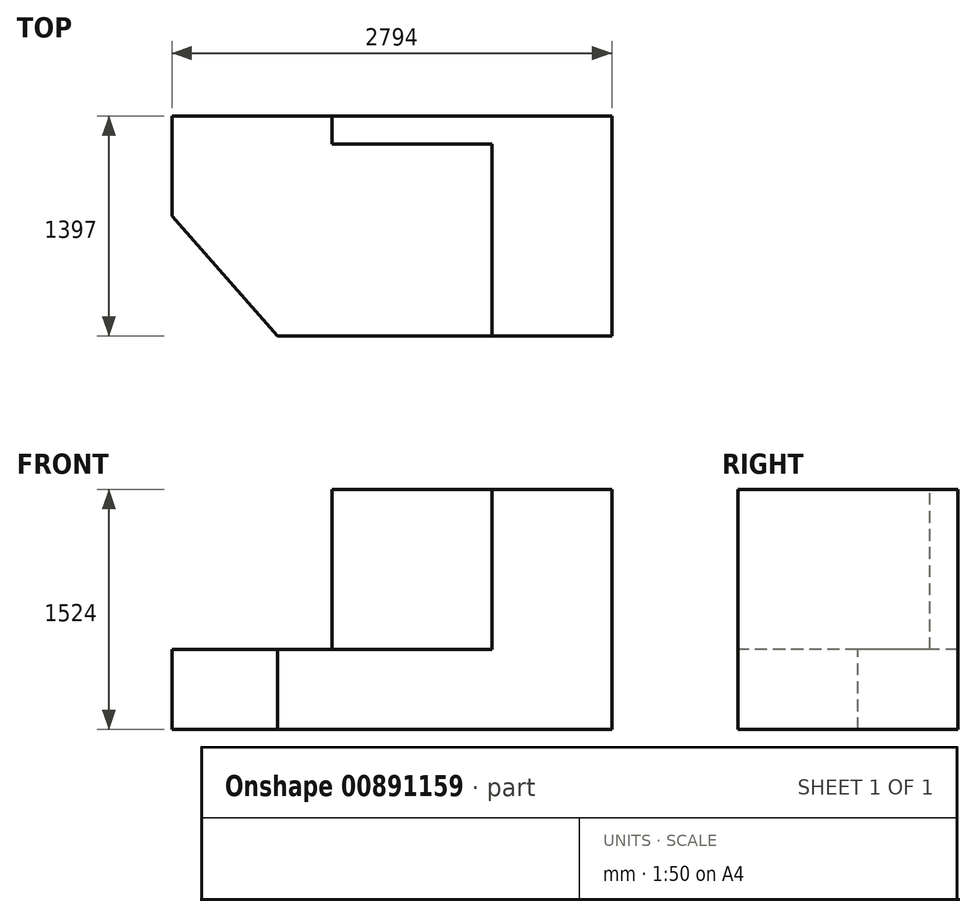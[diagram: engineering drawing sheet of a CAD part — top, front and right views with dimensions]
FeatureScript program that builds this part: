
annotation { "Feature Type Name" : "Feature", "Feature Type Description" : "" }
export const myFeature = defineFeature(function(context is Context, id is Id, definition is map)
    precondition{}
    {
        {
            var Q0;
            Q0=qCreatedBy(makeId("Top.planeOp"),FACE);
            var sketch = newSketch(context, id + "F0", { "sketchPlane" : qUnion([Q0])});
            skLineSegment(sketch, "E0.bottom", {"start": v(0, 0) * mm, "end": v(-2794, 0) * mm});
            skLineSegment(sketch, "E0.top", {"start": v(0, 1397) * mm, "end": v(-2794, 1397) * mm});
            skLineSegment(sketch, "E0.left", {"start": v(0, 0) * mm, "end": v(0, 1397) * mm});
            skLineSegment(sketch, "E0.right", {"start": v(-2794, 0) * mm, "end": v(-2794, 1397) * mm});
            skSolve(sketch);
        }
        {
            var Q0;
            Q0 = qSketchRegion(id + "F0", true);
            extrude(context, id + "F1", {"entities" : qUnion([Q0]), "depth" : 1524 * mm, "offsetDistance" : 25.4 * mm});
        }
        {
            var Q0;
            Q0=makeQuery(id+"F1.opExtrude","CAP_FACE",FACE,{"disambiguationData":[OSD([sQuery(id+"F0.wireOp",EDGE,"E0.bottom"),sQuery(id+"F0.wireOp",EDGE,"E0.top"),sQuery(id+"F0.wireOp",EDGE,"E0.left"),sQuery(id+"F0.wireOp",EDGE,"E0.right")])],"isStart":false});
            var sketch = newSketch(context, id + "F2", { "sketchPlane" : qUnion([Q0])});
            skLineSegment(sketch, "E1.bottom", {"start": v(-1778, 1397) * mm, "end": v(0, 1397) * mm});
            skLineSegment(sketch, "E1.top", {"start": v(-1778, 1219.2) * mm, "end": v(0, 1219.2) * mm});
            skLineSegment(sketch, "E1.left", {"start": v(-1778, 1397) * mm, "end": v(-1778, 1219.2) * mm});
            skLineSegment(sketch, "E1.right", {"start": v(0, 1397) * mm, "end": v(0, 1219.2) * mm});
            skSolve(sketch);
        }
        {
            var Q0;
            {var subQ4=sQuery(id+"F2.wireOp",EDGE,"E1.top");Q0=makeQuery(id+"F2.imprint","IMPRINT",FACE,{"disambiguationData":[TD([[makeQuery(id+"F2.imprint","IMPRINT",EDGE,{"derivedFrom":subQ4}),-1.0]])]});}
            var sketch = newSketch(context, id + "F3", { "sketchPlane" : qUnion([Q0])});
            skLineSegment(sketch, "E2.bottom", {"start": v(-762, 1016) * mm, "end": v(0, 1016) * mm});
            skLineSegment(sketch, "E2.top", {"start": v(-762, 0) * mm, "end": v(0, 0) * mm});
            skLineSegment(sketch, "E2.left", {"start": v(-762, 1016) * mm, "end": v(-762, 0) * mm});
            skLineSegment(sketch, "E2.right", {"start": v(0, 1016) * mm, "end": v(0, 0) * mm});
            skLineSegment(sketch, "E3.bottom", {"start": v(-1775.76, 1225.1) * mm, "end": v(-762, 1225.1) * mm});
            skLineSegment(sketch, "E3.top", {"start": v(-1775.76, 0) * mm, "end": v(-762, 0) * mm});
            skLineSegment(sketch, "E3.left", {"start": v(-1775.76, 1225.1) * mm, "end": v(-1775.76, 0) * mm});
            skLineSegment(sketch, "E3.right", {"start": v(-762, 1225.1) * mm, "end": v(-762, 0) * mm});
            skSolve(sketch);
        }
        {
            var Q0;
            {var subQ5=sQuery(id+"F3.wireOp",EDGE,"E3.top");Q0=makeQuery(id+"F3.imprint","IMPRINT",FACE,{"disambiguationData":[TD([[makeQuery(id+"F3.imprint","IMPRINT",EDGE,{"derivedFrom":subQ5}),-1.0]])]});}
            extrude(context, id + "F4", {"entities" : qUnion([Q0]), "operationType" : NewBodyOperationType.REMOVE, "oppositeDirection" : true, "depth" : 1016 * mm, "offsetDistance" : 25.4 * mm});
        }
        {
            var Q0;
            Q0=makeQuery(id+"F1.opExtrude","SWEPT_FACE",FACE,{"disambiguationData":[OSD([sQuery(id+"F0.wireOp",EDGE,"E0.bottom")])]});
            var sketch = newSketch(context, id + "F5", { "sketchPlane" : qUnion([Q0])});
            skLineSegment(sketch, "E4.bottom", {"start": v(-1775.76, 508) * mm, "end": v(-2794, 508) * mm});
            skLineSegment(sketch, "E4.top", {"start": v(-1775.76, 1524) * mm, "end": v(-2794, 1524) * mm});
            skLineSegment(sketch, "E4.left", {"start": v(-1775.76, 508) * mm, "end": v(-1775.76, 1524) * mm});
            skLineSegment(sketch, "E4.right", {"start": v(-2794, 508) * mm, "end": v(-2794, 1524) * mm});
            skSolve(sketch);
        }
        {
            var Q0;
            Q0=makeQuery(id+"F5.imprint","IMPRINT",FACE,{"disambiguationData":[TD([[makeQuery(id+"F5.imprint","IMPRINT",EDGE,{"derivedFrom":sQuery(id+"F5.wireOp",EDGE,"E4.bottom")}),-1.0]])]});
            extrude(context, id + "F6", {"entities" : qUnion([Q0]), "operationType" : NewBodyOperationType.REMOVE, "oppositeDirection" : true, "depth" : 3329.94 * mm, "offsetDistance" : 25.4 * mm});
        }
        {
            var Q0;
            Q0=makeQuery(id+"F6.boolean.opBoolean","MERGE",FACE,{"derivedFrom":[makeQuery(id+"F4.boolean.opBoolean","COPY",FACE,{"derivedFrom":makeQuery(id+"F4.opExtrude","CAP_FACE",FACE,{"disambiguationData":[OSD([sQuery(id+"F2.wireOp",EDGE,"E1.top"),sQuery(id+"F3.wireOp",EDGE,"E3.top"),sQuery(id+"F3.wireOp",EDGE,"E3.left"),sQuery(id+"F3.wireOp",EDGE,"E3.right")])],"isStart":false})})],"fromTools":[makeQuery(id+"F6.opExtrude","SWEPT_FACE",FACE,{"disambiguationData":[OSD([sQuery(id+"F5.wireOp",EDGE,"E4.bottom")])]})]});
            var sketch = newSketch(context, id + "F7", { "sketchPlane" : qUnion([Q0])});
            skLineSegment(sketch, "E5", {"start": v(-2794, 1397) * mm, "end": v(-2794, 762) * mm});
            skLineSegment(sketch, "E6", {"start": v(-2794, 762) * mm, "end": v(-2121.98, 0) * mm});
            skSolve(sketch);
        }
        {
            var Q0;
            {var subQ0=sQuery(id+"F7.wireOp",EDGE,"E6");Q0=makeQuery(id+"F7.imprint","IMPRINT",FACE,{"disambiguationData":[TD([[makeQuery(id+"F7.imprint","IMPRINT",EDGE,{"derivedFrom":subQ0}),-1.0]])]});}
            extrude(context, id + "F8", {"entities" : qUnion([Q0]), "operationType" : NewBodyOperationType.REMOVE, "oppositeDirection" : true, "depth" : 1772.92 * mm, "offsetDistance" : 25.4 * mm});
        }
    });
